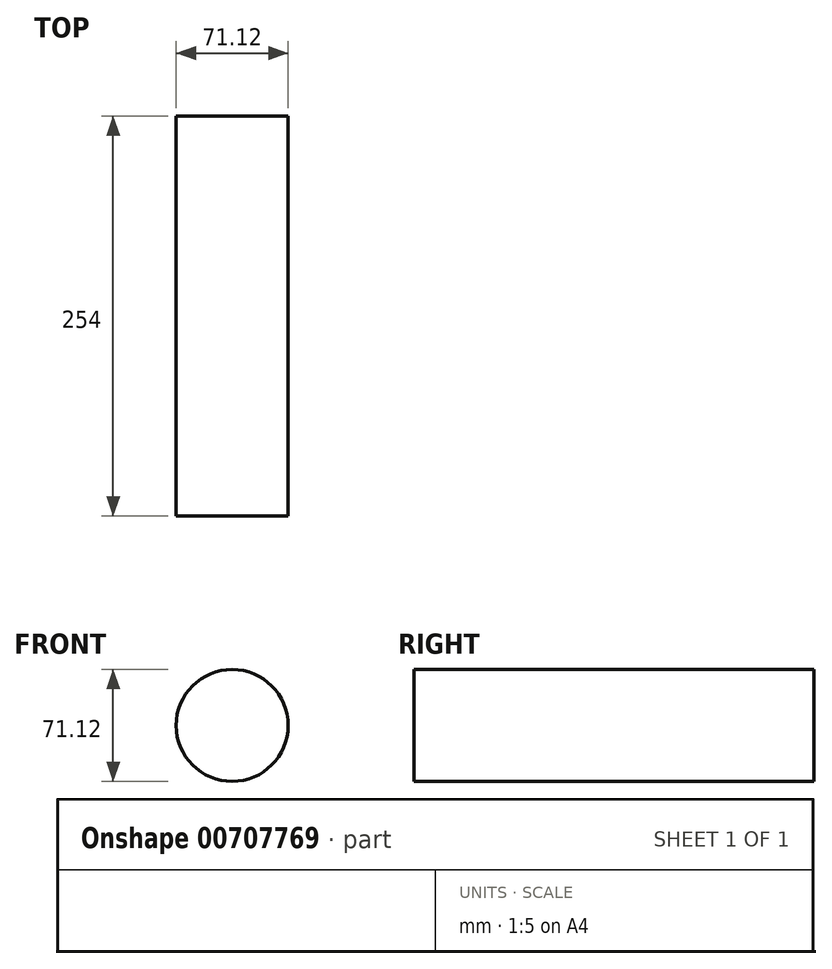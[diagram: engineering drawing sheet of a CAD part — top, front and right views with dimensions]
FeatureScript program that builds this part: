
annotation { "Feature Type Name" : "Feature", "Feature Type Description" : "" }
export const myFeature = defineFeature(function(context is Context, id is Id, definition is map)
    precondition{}
    {
        {
            var Q0;
            Q0=qCreatedBy(makeId("Front.planeOp"),FACE);
            var sketch = newSketch(context, id + "F0", { "sketchPlane" : qUnion([Q0])});
            skCircle(sketch, "E0", {"center": v(20.41, 13.37) * mm, "radius": 35.56 * mm});
            skSolve(sketch);
        }
        {
            var Q0;
            Q0=makeQuery(id+"F0.imprint","IMPRINT",FACE,{"disambiguationData":[TD([[makeQuery(id+"F0.imprint","IMPRINT",EDGE,{"derivedFrom":sQuery(id+"F0.wireOp",EDGE,"E0")}),1.0]])]});
            extrude(context, id + "F1", {"entities" : qUnion([Q0]), "depth" : 254 * mm, "offsetDistance" : 25.4 * mm});
        }
    });
